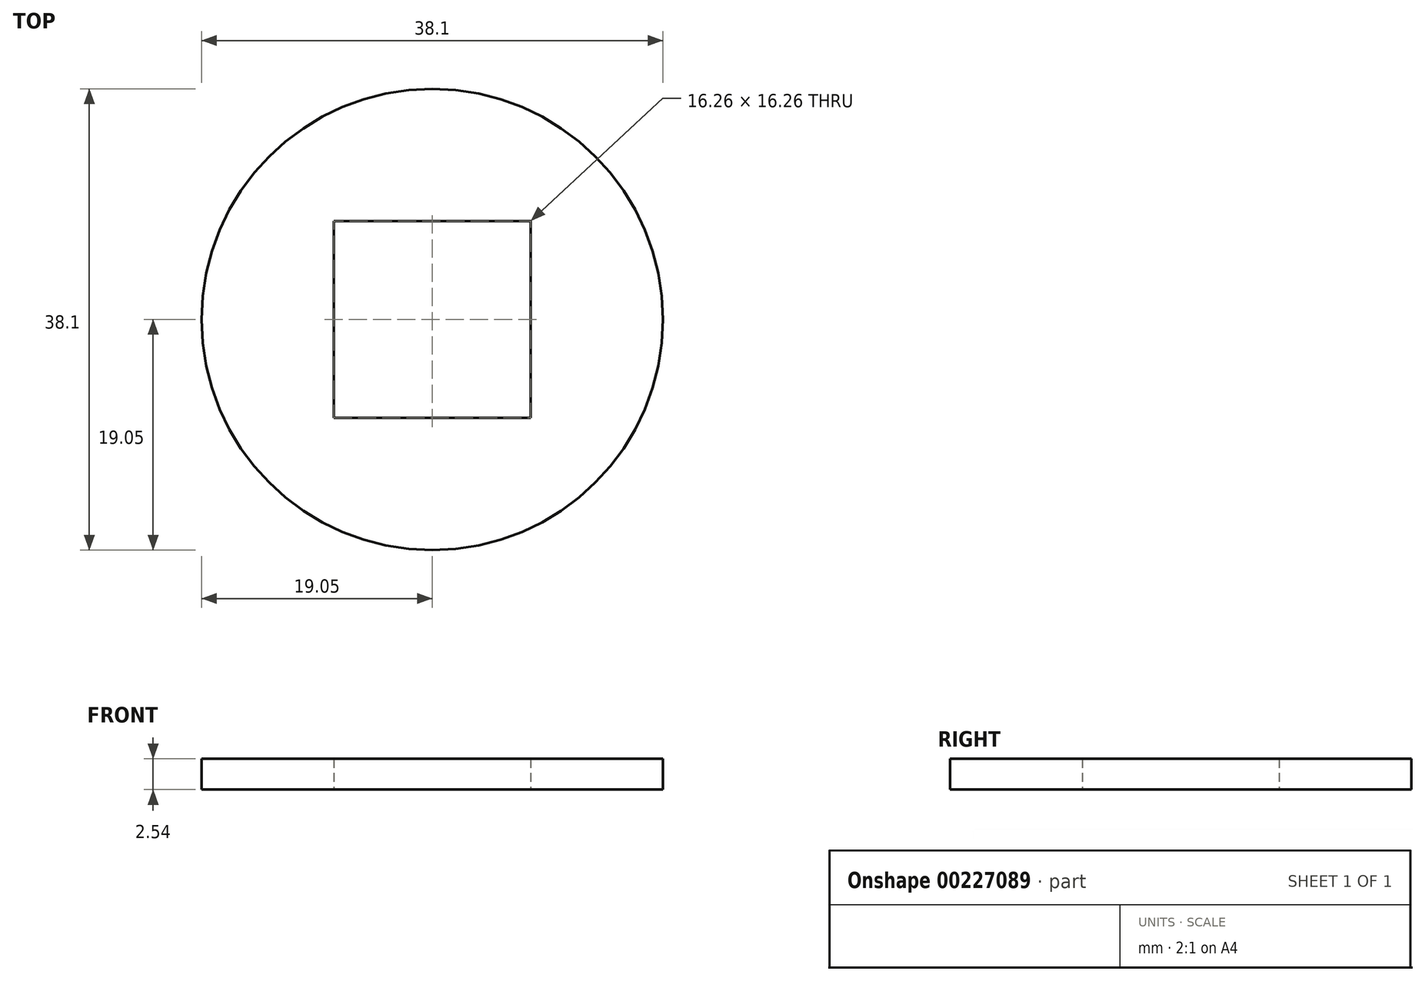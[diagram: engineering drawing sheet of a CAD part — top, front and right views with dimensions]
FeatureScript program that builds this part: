
annotation { "Feature Type Name" : "Feature", "Feature Type Description" : "" }
export const myFeature = defineFeature(function(context is Context, id is Id, definition is map)
    precondition{}
    {
        {
            var Q0;
            Q0=qCreatedBy(makeId("Top.planeOp"),FACE);
            var sketch = newSketch(context, id + "F0", { "sketchPlane" : qUnion([Q0])});
            skCircle(sketch, "E0", {"center": v(0, 0) * mm, "radius": 19.05 * mm});
            skLineSegment(sketch, "E1.bottom", {"start": v(-8.13, 8.13) * mm, "end": v(8.13, 8.13) * mm});
            skLineSegment(sketch, "E1.top", {"start": v(-8.13, -8.13) * mm, "end": v(8.13, -8.13) * mm});
            skLineSegment(sketch, "E1.left", {"start": v(-8.13, 8.13) * mm, "end": v(-8.13, -8.13) * mm});
            skLineSegment(sketch, "E1.right", {"start": v(8.13, 8.13) * mm, "end": v(8.13, -8.13) * mm});
            skLineSegment(sketch, "E2.bottom", {"start": v(-6.6, 6.6) * mm, "end": v(6.6, 6.6) * mm});
            skLineSegment(sketch, "E2.top", {"start": v(-6.6, -6.6) * mm, "end": v(6.6, -6.6) * mm});
            skLineSegment(sketch, "E2.left", {"start": v(-6.6, 6.6) * mm, "end": v(-6.6, -6.6) * mm});
            skLineSegment(sketch, "E2.right", {"start": v(6.6, 6.6) * mm, "end": v(6.6, -6.6) * mm});
            skSolve(sketch);
        }
        {
            var Q0;
            Q0 = qSketchRegion(id + "F0", true);
            extrude(context, id + "F1", {"entities" : qUnion([Q0]), "depth" : 2.54 * mm});
        }
    });
